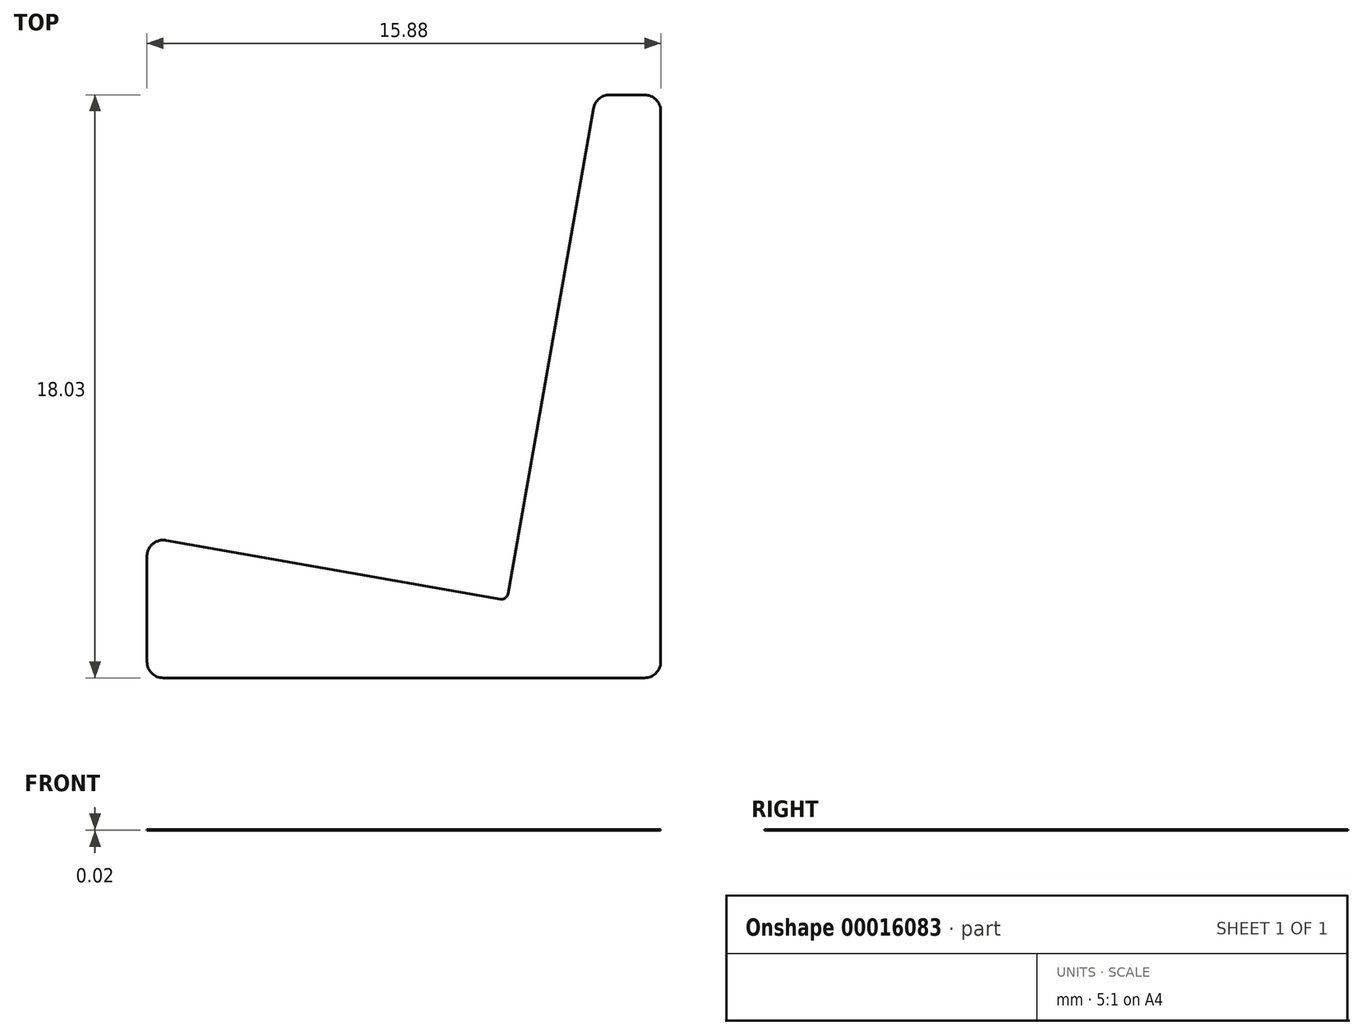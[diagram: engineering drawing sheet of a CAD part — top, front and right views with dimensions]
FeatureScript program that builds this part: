
annotation { "Feature Type Name" : "Feature", "Feature Type Description" : "" }
export const myFeature = defineFeature(function(context is Context, id is Id, definition is map)
    precondition{}
    {
        {
            var Q0;
            Q0=qCreatedBy(makeId("Top.planeOp"),FACE);
            var sketch = newSketch(context, id + "F0", { "sketchPlane" : qUnion([Q0])});
            skLineSegment(sketch, "E0", {"start": v(2.98, 2.43) * mm, "end": v(-7.35, 4.26) * mm});
            skLineSegment(sketch, "E1", {"start": v(-7.94, 3.76) * mm, "end": v(-7.94, 0) * mm});
            skLineSegment(sketch, "E2", {"start": v(-7.94, 0) * mm, "end": v(7.94, 0) * mm});
            skLineSegment(sketch, "E3", {"start": v(7.94, 0) * mm, "end": v(7.94, 17.53) * mm});
            skLineSegment(sketch, "E4", {"start": v(3.22, 2.6) * mm, "end": v(5.86, 17.62) * mm});
            skLineSegment(sketch, "E5", {"start": v(6.36, 18.03) * mm, "end": v(7.44, 18.03) * mm});
            skPoint(sketch, "E6.visualSharp", {"position": v(5.94, 18.03) * mm});
            skArc(sketch, "E6.filletArc", {"start": v(6.36, 18.03) * mm, "mid": v(6.04, 17.92) * mm, "end": v(5.86, 17.62) * mm});
            skPoint(sketch, "E7.visualSharp", {"position": v(7.94, 18.03) * mm});
            skArc(sketch, "E7.filletArc", {"start": v(7.94, 17.53) * mm, "mid": v(7.8, 17.89) * mm, "end": v(7.44, 18.03) * mm});
            skPoint(sketch, "E8.visualSharp", {"position": v(-7.94, 4.36) * mm});
            skArc(sketch, "E8.filletArc", {"start": v(-7.35, 4.26) * mm, "mid": v(-7.76, 4.15) * mm, "end": v(-7.94, 3.76) * mm});
            skPoint(sketch, "E9.visualSharp", {"position": v(3.18, 2.4) * mm});
            skArc(sketch, "E9.filletArc", {"start": v(2.98, 2.43) * mm, "mid": v(3.13, 2.47) * mm, "end": v(3.22, 2.6) * mm});
            skSolve(sketch);
        }
        {
            var Q0;
            Q0=qSketchRegion(id+"F0",true);
            var Q1;
            Q1=makeQuery(id+"F0.imprint","IMPRINT",FACE,{"disambiguationData":[TD([[makeQuery(id+"F0.imprint","IMPRINT",EDGE,{"derivedFrom":sQuery(id+"F0.wireOp",EDGE,"0de830e7-9daf-4a68-be67-74efd37edb9d.0")}),-1.0]])]});
            extrude(context, id + "F1", {"entities" : qUnion([Q0, Q1]), "depth" : 5 / 203.2 * mm});
        }
        {
            var Q0;
            Q0=makeQuery(id+"F1.opExtrude","SWEPT_EDGE",EDGE,{"disambiguationData":[OSD([sQuery(id+"F0.wireOp",EDGE,"E4"),sQuery(id+"F0.wireOp",EDGE,"E5")])]});
            var Q1;
            Q1=makeQuery(id+"F1.opExtrude","SWEPT_EDGE",EDGE,{"disambiguationData":[OSD([sQuery(id+"F0.wireOp",EDGE,"E0"),sQuery(id+"F0.wireOp",EDGE,"E1")])]});
            var Q2;
            Q2=makeQuery(id+"F1.opExtrude","SWEPT_EDGE",EDGE,{"disambiguationData":[OSD([sQuery(id+"F0.wireOp",EDGE,"E3"),sQuery(id+"F0.wireOp",EDGE,"E5")])]});
            fillet(context, id + "F2", {"entities" : qUnion([Q0, Q1, Q2]), "radius" : .5 * mm, "tangentPropagation" : true, "allowEdgeOverflow" : false});
        }
    });
